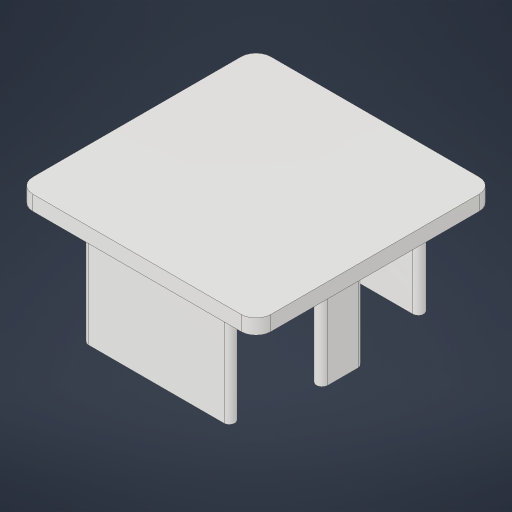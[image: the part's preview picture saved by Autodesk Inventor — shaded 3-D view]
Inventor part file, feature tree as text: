
AUTODESK INVENTOR PART (.ipt)
format: ipt  version: 2023.4 (Build 274418000, 418)  size: 225,792 bytes
history: native  units: in
note: dims shown in document units (in); Inventor stores cm internally (conversion verified against a paired STEP export)
features: extrude x2, fillet x2, sketch x1
ambient origin geometry x8: Origin, YZ Plane, XZ Plane, XY Plane, X Axis, Y Axis, Z Axis, Center Point
bodies: Solid1 (feature_tree)
feature tree (5):
  sketch  "Sketch1"  dims[d0=1.25in d1=2.0in d2=2.0in d3=1.477in d4=0.11in d5=1.25in d6=0.11in d7=0.37in d8=0.115in d10=0.01in d11=0.01in d12=0.125in d13=0.0in d14=0.9in d15=0.0in d16=0.125in d17=0.125in]
  extrude  "Extrusion1"  Depth=2.0in
  extrude  "Extrusion2"  Depth=2.0in
  fillet  "Fillet1"  Radius=1.477in
  fillet  "Fillet2"  Radius=0.11in
